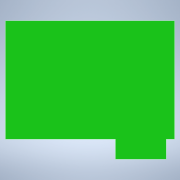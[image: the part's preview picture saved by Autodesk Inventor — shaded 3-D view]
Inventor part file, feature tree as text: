
AUTODESK INVENTOR PART (.ipt)
format: ipt  version: 2022 (Build 260153000, 153)  size: 120,320 bytes
history: native  units: mm
features: sketch x2, extrude x2
ambient origin geometry x8: Origin, YZ Plane, XZ Plane, XY Plane, X Axis, Y Axis, Z Axis, Center Point
bodies: Body1 (feature_tree)
feature tree (4):
  sketch  "Sketch2"  dims[d0=50.0mm d1=35.0mm]
  extrude  "Extrusion12"  Depth=35.0mm
  extrude  "Extrusion13"  Depth=15.0mm
  sketch  "Sketch7"  dims[d58=2.5mm d59=15.0mm d60=6.0mm d68=6.0mm d69=0.0mm d79=0.0mm d80=0.0mm d4=0.0mm d5=0.0mm d6=0.0mm d7=0.0mm]
